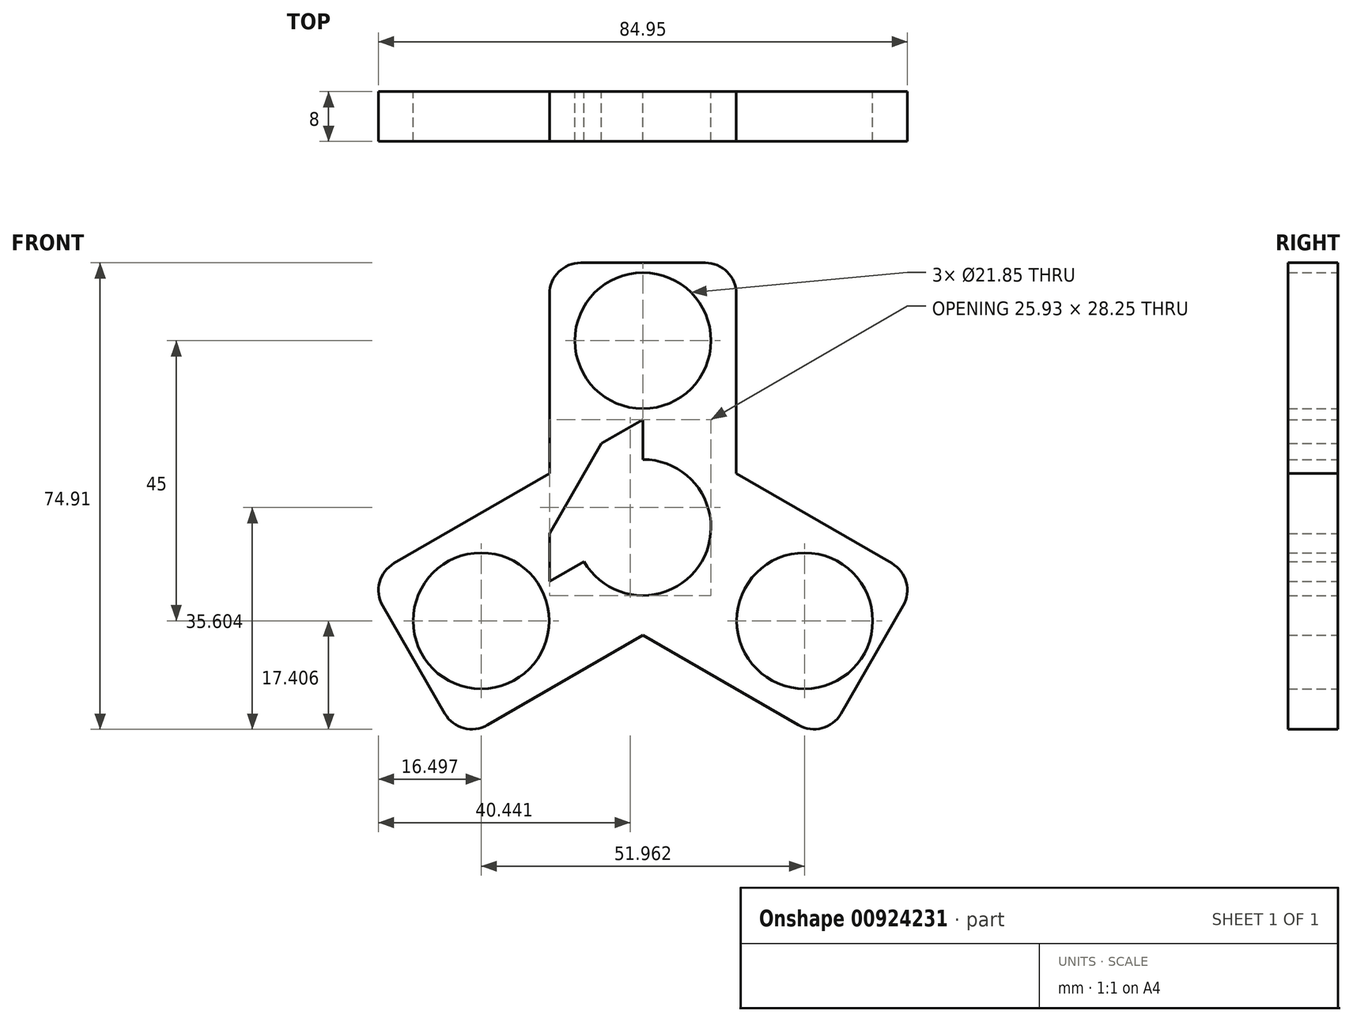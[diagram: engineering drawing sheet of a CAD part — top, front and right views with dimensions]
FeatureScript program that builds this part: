
annotation { "Feature Type Name" : "Feature", "Feature Type Description" : "" }
export const myFeature = defineFeature(function(context is Context, id is Id, definition is map)
    precondition{}
    {
        {
            var Q0;
            Q0=qCreatedBy(makeId("Front.planeOp"),FACE);
            var sketch = newSketch(context, id + "F0", { "sketchPlane" : qUnion([Q0])});
            skCircle(sketch, "E0", {"center": v(-178.7, -12) * mm, "radius": 10.93 * mm});
            skCircle(sketch, "E1", {"center": v(-178.7, 18) * mm, "radius": 10.93 * mm});
            skLineSegment(sketch, "E2", {"start": v(-178.7, 18) * mm, "end": v(-178.7, -12) * mm});
            skPoint(sketch, "E3", {"position": v(-178.7, 3) * mm});
            skLineSegment(sketch, "E4.bottom", {"start": v(-163.7, -24.5) * mm, "end": v(-193.7, -24.5) * mm});
            skLineSegment(sketch, "E4.top", {"start": v(-168.7, 30.5) * mm, "end": v(-188.7, 30.5) * mm});
            skLineSegment(sketch, "E4.left", {"start": v(-163.7, -24.5) * mm, "end": v(-163.7, 25.5) * mm});
            skLineSegment(sketch, "E4.right", {"start": v(-193.7, -24.5) * mm, "end": v(-193.7, 25.5) * mm});
            skPoint(sketch, "E5.visualSharp", {"position": v(-193.7, 30.5) * mm});
            skArc(sketch, "E5.filletArc", {"start": v(-188.7, 30.5) * mm, "mid": v(-192.24, 29.03) * mm, "end": v(-193.7, 25.5) * mm});
            skPoint(sketch, "E6.visualSharp", {"position": v(-163.7, 30.5) * mm});
            skArc(sketch, "E6.filletArc", {"start": v(-163.7, 25.5) * mm, "mid": v(-165.17, 29.03) * mm, "end": v(-168.7, 30.5) * mm});
            skLineSegment(sketch, "E7.1.0", {"start": v(-175.38, 7.24) * mm, "end": v(-218.68, -17.76) * mm});
            skPoint(sketch, "E7.1.1", {"position": v(-208, -46.24) * mm});
            skLineSegment(sketch, "E7.1.2", {"start": v(-204.68, -27) * mm, "end": v(-178.7, -12) * mm});
            skLineSegment(sketch, "E7.1.3", {"start": v(-220.5, -24.6) * mm, "end": v(-210.5, -41.91) * mm});
            skLineSegment(sketch, "E7.1.4", {"start": v(-160.38, -18.74) * mm, "end": v(-203.68, -43.74) * mm});
            skPoint(sketch, "E7.1.5", {"position": v(-223, -20.26) * mm});
            skLineSegment(sketch, "E7.1.7", {"start": v(-175.38, 7.24) * mm, "end": v(-160.38, -18.74) * mm});
            skCircle(sketch, "E7.1.8", {"center": v(-204.68, -27) * mm, "radius": 10.93 * mm});
            skPoint(sketch, "E7.1.9", {"position": v(-191.7, -19.5) * mm});
            skArc(sketch, "E7.1.10", {"start": v(-218.68, -17.76) * mm, "mid": v(-221, -20.8) * mm, "end": v(-220.5, -24.6) * mm});
            skPoint(sketch, "E7.1.11", {"position": v(-191.7, -19.5) * mm});
            skArc(sketch, "E7.1.12", {"start": v(-210.5, -41.91) * mm, "mid": v(-207.47, -44.24) * mm, "end": v(-203.68, -43.74) * mm});
            skLineSegment(sketch, "E7.2.0", {"start": v(-197.03, -18.74) * mm, "end": v(-153.73, -43.74) * mm});
            skPoint(sketch, "E7.2.1", {"position": v(-134.4, -20.26) * mm});
            skLineSegment(sketch, "E7.2.2", {"start": v(-152.72, -27) * mm, "end": v(-178.7, -12) * mm});
            skLineSegment(sketch, "E7.2.3", {"start": v(-146.9, -41.91) * mm, "end": v(-136.9, -24.6) * mm});
            skLineSegment(sketch, "E7.2.4", {"start": v(-182.03, 7.24) * mm, "end": v(-138.73, -17.76) * mm});
            skPoint(sketch, "E7.2.5", {"position": v(-149.4, -46.24) * mm});
            skLineSegment(sketch, "E7.2.7", {"start": v(-197.03, -18.74) * mm, "end": v(-182.03, 7.24) * mm});
            skCircle(sketch, "E7.2.8", {"center": v(-152.72, -27) * mm, "radius": 10.93 * mm});
            skPoint(sketch, "E7.2.9", {"position": v(-165.71, -19.5) * mm});
            skArc(sketch, "E7.2.10", {"start": v(-153.73, -43.74) * mm, "mid": v(-149.93, -44.24) * mm, "end": v(-146.9, -41.91) * mm});
            skPoint(sketch, "E7.2.11", {"position": v(-165.71, -19.5) * mm});
            skArc(sketch, "E7.2.12", {"start": v(-136.9, -24.6) * mm, "mid": v(-136.4, -20.8) * mm, "end": v(-138.73, -17.76) * mm});
            skSolve(sketch);
        }
        {
            var Q0;
            Q0 = qSketchRegion(id + "F0", true);
            var Q1;
            {var subQ3=sQuery(id+"F0.wireOp",EDGE,"E2");var subQ9=sQuery(id+"F0.wireOp",EDGE,"E0");var subQ10=makeQuery(id+"F0.imprint","INTERSECT",VERTEX,{"derivedFrom":[subQ3,subQ9]});Q1=makeQuery(id+"F0.imprint","IMPRINT",FACE,{"disambiguationData":[TD([[makeQuery(id+"F0.imprint","IMPRINT",EDGE,{"disambiguationData":[TD([[subQ10,-1.0]])],"derivedFrom":subQ9}),-1.0]])]});}
            var Q2;
            {var subQ0=sQuery(id+"F0.wireOp",EDGE,"E7.1.7");var subQ1=sQuery(id+"F0.wireOp",EDGE,"E4.left");var subQ2=makeQuery(id+"F0.imprint","INTERSECT",VERTEX,{"derivedFrom":[subQ1,subQ0]});Q2=makeQuery(id+"F0.imprint","IMPRINT",FACE,{"disambiguationData":[TD([[makeQuery(id+"F0.imprint","IMPRINT",EDGE,{"disambiguationData":[TD([[subQ2,1.0]])],"derivedFrom":subQ0}),-1.0]])]});}
            var Q3;
            {var subQ0=sQuery(id+"F0.wireOp",EDGE,"E7.1.7");var subQ1=sQuery(id+"F0.wireOp",EDGE,"E7.1.0");var subQ2=makeQuery(id+"F0.imprint","INTERSECT",VERTEX,{"derivedFrom":[subQ1,subQ0]});Q3=makeQuery(id+"F0.imprint","IMPRINT",FACE,{"disambiguationData":[TD([[makeQuery(id+"F0.imprint","IMPRINT",EDGE,{"disambiguationData":[TD([[subQ2,-1.0]])],"derivedFrom":subQ0}),-1.0]])]});}
            var Q4;
            {var subQ0=sQuery(id+"F0.wireOp",EDGE,"E7.2.7");var subQ3=sQuery(id+"F0.wireOp",EDGE,"E7.2.4");var subQ5=makeQuery(id+"F0.imprint","INTERSECT",VERTEX,{"derivedFrom":[subQ3,subQ0]});Q4=makeQuery(id+"F0.imprint","IMPRINT",FACE,{"disambiguationData":[TD([[makeQuery(id+"F0.imprint","IMPRINT",EDGE,{"disambiguationData":[TD([[subQ5,1.0]])],"derivedFrom":subQ0}),-1.0]])]});}
            var Q5;
            {var subQ1=sQuery(id+"F0.wireOp",EDGE,"E4.bottom");var subQ5=sQuery(id+"F0.wireOp",EDGE,"E7.1.4");var subQ6=makeQuery(id+"F0.imprint","INTERSECT",VERTEX,{"derivedFrom":[subQ1,subQ5]});Q5=makeQuery(id+"F0.imprint","IMPRINT",FACE,{"disambiguationData":[TD([[makeQuery(id+"F0.imprint","IMPRINT",EDGE,{"disambiguationData":[TD([[subQ6,-1.0]])],"derivedFrom":subQ1}),-1.0]])]});}
            var Q6;
            {var subQ0=sQuery(id+"F0.wireOp",EDGE,"E7.1.7");var subQ3=sQuery(id+"F0.wireOp",EDGE,"E7.1.4");var subQ5=makeQuery(id+"F0.imprint","INTERSECT",VERTEX,{"derivedFrom":[subQ3,subQ0]});Q6=makeQuery(id+"F0.imprint","IMPRINT",FACE,{"disambiguationData":[TD([[makeQuery(id+"F0.imprint","IMPRINT",EDGE,{"disambiguationData":[TD([[subQ5,1.0]])],"derivedFrom":subQ0}),-1.0]])]});}
            var Q7;
            {var subQ0=sQuery(id+"F0.wireOp",EDGE,"E4.left");var subQ1=sQuery(id+"F0.wireOp",EDGE,"E4.bottom");var subQ2=makeQuery(id+"F0.imprint","INTERSECT",VERTEX,{"derivedFrom":[subQ1,subQ0]});Q7=makeQuery(id+"F0.imprint","IMPRINT",FACE,{"disambiguationData":[TD([[makeQuery(id+"F0.imprint","IMPRINT",EDGE,{"disambiguationData":[TD([[subQ2,-1.0]])],"derivedFrom":subQ1}),-1.0]])]});}
            var Q8;
            {var subQ0=sQuery(id+"F0.wireOp",EDGE,"E4.right");var subQ1=sQuery(id+"F0.wireOp",EDGE,"E4.bottom");var subQ2=makeQuery(id+"F0.imprint","INTERSECT",VERTEX,{"derivedFrom":[subQ1,subQ0]});Q8=makeQuery(id+"F0.imprint","IMPRINT",FACE,{"disambiguationData":[TD([[makeQuery(id+"F0.imprint","IMPRINT",EDGE,{"disambiguationData":[TD([[subQ2,1.0]])],"derivedFrom":subQ1}),-1.0]])]});}
            var Q9;
            {var subQ0=sQuery(id+"F0.wireOp",EDGE,"E7.2.7");var subQ3=sQuery(id+"F0.wireOp",EDGE,"E7.2.0");var subQ5=makeQuery(id+"F0.imprint","INTERSECT",VERTEX,{"derivedFrom":[subQ3,subQ0]});Q9=makeQuery(id+"F0.imprint","IMPRINT",FACE,{"disambiguationData":[TD([[makeQuery(id+"F0.imprint","IMPRINT",EDGE,{"disambiguationData":[TD([[subQ5,-1.0]])],"derivedFrom":subQ0}),-1.0]])]});}
            extrude(context, id + "F1", {"entities" : qUnion([Q0, Q1, Q2, Q3, Q4, Q5, Q6, Q7, Q8, Q9]), "depth" : 8 * mm, "offsetDistance" : 25 * mm});
        }
    });
